# Revit family: Sink-Under_Counter-Kohler-Prolific-5540
name_source: partatom
category: Plumbing Fixtures
revit_build: Autodesk Revit MEP 2012 (Build: 20110916_2132(x64)
units: mm (PartAtom-declared; Revit-internal decimal feet)

## types (1)
- Single-Bowl Sink
    Date Modified = March 13, 2015
    Depth = 17.75 "
    Description = Prolific Under-Mount Single-Bowl Kitchen Sink With Accessories
    Drain Flow = 0 GPM
    Drain Radius = 0.75 "
    Equipment Abbreviation = PUM
    Family Version = 1.0
    Height = 10.938 "
    Manufacturer = Kohler Company
    Model = K-5540-NA
    Model Disclaimer = Contact Kohler Company For More Information
    Product Material = Stainless Steel - Kohler - Polished
    Product Page URL = http://www.us.kohler.com
    URL = http://www.us.kohler.com
    Width = 33 "
    zz Length 1 = 11 "
    zz Length 11 = 8.1 "
    zz Length 12 = 33 "
    zz Length 13 = 10.938 "
    zz Length 15 = 21.5 "
    zz Length 2 = 0.5 "
    zz Length 3 = 17.75 "
    zz Length 4 = 1.25 "
    zz Length 5 = 0.5 "
    zz Length 6 = 1 "
    zz Length 7 = 3.9 "
    zz Length 8 = 21.5 "
    zz Length 9 = 3.9 "

## geometry (parser evidence)
native form markers: Blend x4, Sweep x2
no freeform markers — native parametric forms only
